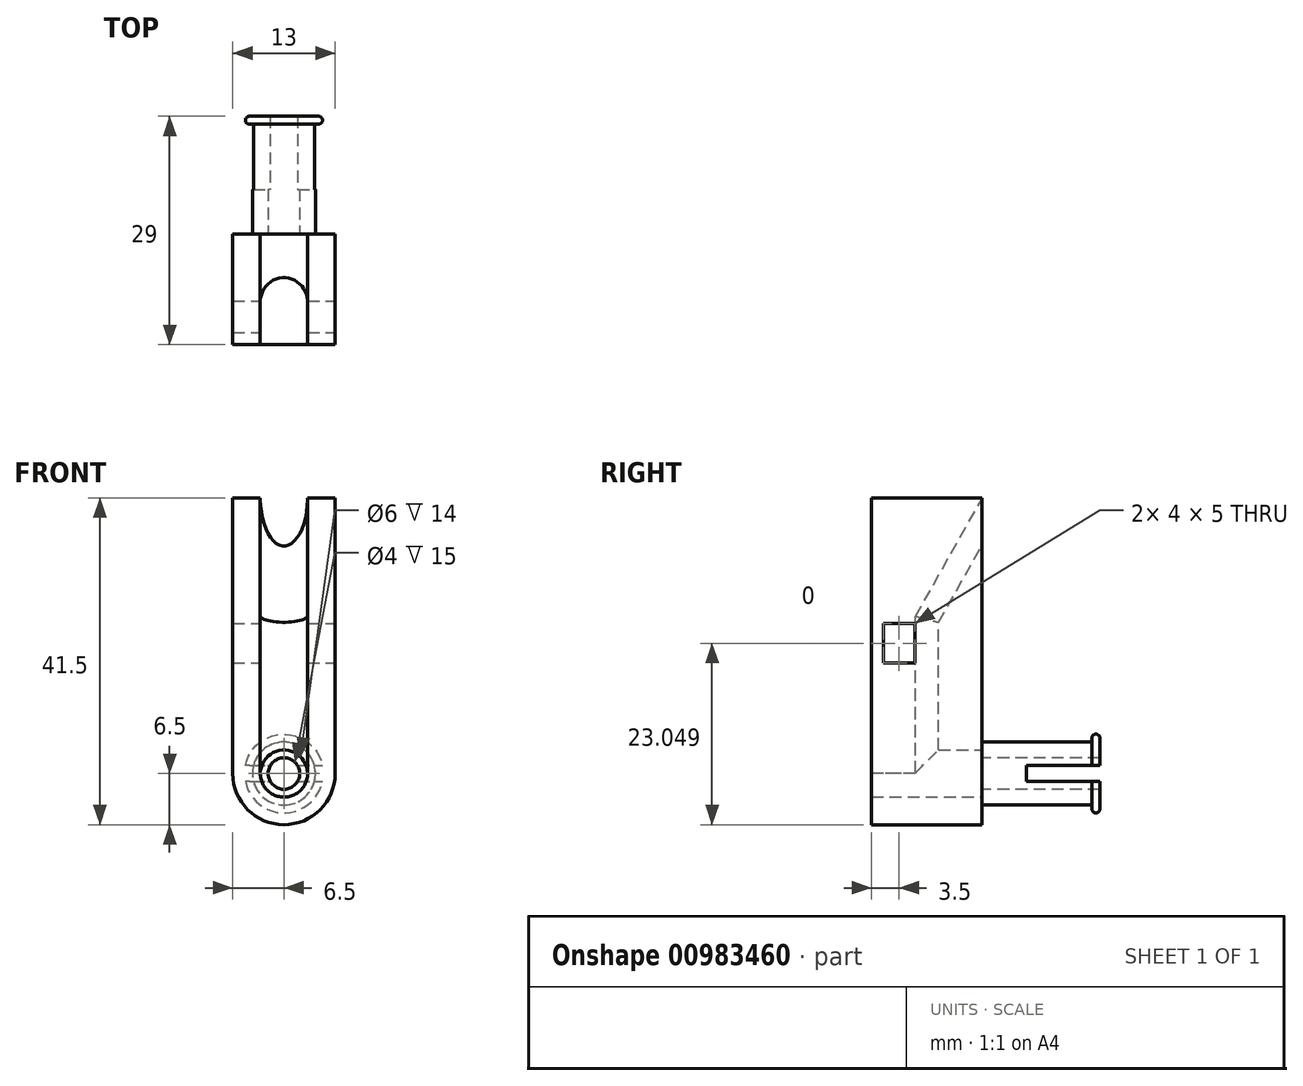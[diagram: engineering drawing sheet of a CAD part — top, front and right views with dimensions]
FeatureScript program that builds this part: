
annotation { "Feature Type Name" : "Feature", "Feature Type Description" : "" }
export const myFeature = defineFeature(function(context is Context, id is Id, definition is map)
    precondition{}
    {
        {
            var Q0;
            Q0=qCreatedBy(makeId("Front.planeOp"),FACE);
            var sketch = newSketch(context, id + "F0", { "sketchPlane" : qUnion([Q0])});
            skCircle(sketch, "E0", {"center": v(0, 0) * mm, "radius": 4 * mm});
            skCircle(sketch, "E1", {"center": v(0, 0) * mm, "radius": 6.5 * mm});
            skPoint(sketch, "E2.middle", {"position": v(0, -6.5) * mm});
            skCircle(sketch, "E3", {"center": v(0, 0) * mm, "radius": 5 * mm});
            skLineSegment(sketch, "E4.bottom", {"start": v(6.5, 0) * mm, "end": v(-6.5, 0) * mm});
            skLineSegment(sketch, "E4.top", {"start": v(6.5, 35) * mm, "end": v(-6.5, 35) * mm});
            skLineSegment(sketch, "E4.left", {"start": v(6.5, 0) * mm, "end": v(6.5, 35) * mm});
            skLineSegment(sketch, "E4.right", {"start": v(-6.5, 0) * mm, "end": v(-6.5, 35) * mm});
            skLineSegment(sketch, "E5.bottom", {"start": v(0, -4) * mm, "end": v(8, -4) * mm});
            skLineSegment(sketch, "E5.top", {"start": v(0, 4) * mm, "end": v(8, 4) * mm});
            skLineSegment(sketch, "E5.left", {"start": v(0, -4) * mm, "end": v(0, 4) * mm});
            skLineSegment(sketch, "E5.right", {"start": v(8, -4) * mm, "end": v(8, 4) * mm});
            skCircle(sketch, "E6", {"center": v(0, 0) * mm, "radius": 3 * mm});
            skCircle(sketch, "E7", {"center": v(4.3, 17.8) * mm, "radius": 1 * mm});
            skCircle(sketch, "E8", {"center": v(3.96, 8.34) * mm, "radius": 1 * mm});
            skCircle(sketch, "E9", {"center": v(0, 0) * mm, "radius": 2 * mm});
            skSolve(sketch);
        }
        {
            var Q0;
            Q0=qCreatedBy(makeId("Right.planeOp"),FACE);
            var sketch = newSketch(context, id + "F1", { "sketchPlane" : qUnion([Q0])});
            skLineSegment(sketch, "E10", {"start": v(0, 40) * mm, "end": v(0, 35) * mm});
            skLineSegment(sketch, "E11", {"start": v(0, 35) * mm, "end": v(-8.5, 20) * mm});
            skLineSegment(sketch, "E12", {"start": v(-8.5, 20) * mm, "end": v(-8.5, 0) * mm});
            skLineSegment(sketch, "E13", {"start": v(-8.5, 0) * mm, "end": v(8.5, 0) * mm});
            skLineSegment(sketch, "E14.left", {"start": v(-6, 2.5) * mm, "end": v(-6, -2.5) * mm});
            skPoint(sketch, "E14.middle", {"position": v(-8.5, 0) * mm});
            skLineSegment(sketch, "E15.bottom", {"start": v(-6, 2.5) * mm, "end": v(-16.53, 2.5) * mm});
            skLineSegment(sketch, "E15.top", {"start": v(-6, -2.5) * mm, "end": v(-16.53, -2.5) * mm});
            skLineSegment(sketch, "E15.right", {"start": v(-16.53, 2.5) * mm, "end": v(-16.53, -2.5) * mm});
            skLineSegment(sketch, "E16.bottom", {"start": v(5.69, 1) * mm, "end": v(25.69, 1) * mm});
            skLineSegment(sketch, "E16.top", {"start": v(5.69, -1) * mm, "end": v(25.69, -1) * mm});
            skLineSegment(sketch, "E16.left", {"start": v(5.69, 1) * mm, "end": v(5.69, -1) * mm});
            skLineSegment(sketch, "E16.right", {"start": v(25.69, 1) * mm, "end": v(25.69, -1) * mm});
            skLineSegment(sketch, "E17.bottom", {"start": v(-8.5, 14.05) * mm, "end": v(-12.5, 14.05) * mm});
            skLineSegment(sketch, "E17.top", {"start": v(-8.5, 19.05) * mm, "end": v(-12.5, 19.05) * mm});
            skLineSegment(sketch, "E17.left", {"start": v(-8.5, 14.05) * mm, "end": v(-8.5, 19.05) * mm});
            skLineSegment(sketch, "E17.right", {"start": v(-12.5, 14.05) * mm, "end": v(-12.5, 19.05) * mm});
            skSolve(sketch);
        }
        {
            var Q0;
            Q0=qCreatedBy(makeId("Top.planeOp"),FACE);
            var sketch = newSketch(context, id + "F2", { "sketchPlane" : qUnion([Q0])});
            skCircle(sketch, "E18", {"center": v(0, -8.5) * mm, "radius": 3 * mm});
            skLineSegment(sketch, "E19.left", {"start": v(0, -5.5) * mm, "end": v(0, -10.5) * mm});
            skLineSegment(sketch, "E20.bottom", {"start": v(-3, -8.42) * mm, "end": v(3, -8.42) * mm});
            skLineSegment(sketch, "E20.top", {"start": v(-3, -23.42) * mm, "end": v(3, -23.42) * mm});
            skLineSegment(sketch, "E20.left", {"start": v(-3, -8.42) * mm, "end": v(-3, -23.42) * mm});
            skLineSegment(sketch, "E20.right", {"start": v(3, -8.42) * mm, "end": v(3, -23.42) * mm});
            skSolve(sketch);
        }
        {
            var Q0;
            Q0=makeQuery(id+"F0.imprint","IMPRINT",FACE,{"disambiguationData":[TD([[makeQuery(id+"F0.imprint","IMPRINT",EDGE,{"derivedFrom":sQuery(id+"F0.wireOp",EDGE,"E0")}),1.0]])]});
            var Q1;
            {var subQ0=sQuery(id+"F0.wireOp",EDGE,"E9");var subQ1=sQuery(id+"F0.wireOp",EDGE,"E4.bottom");var subQ2=makeQuery(id+"F0.imprint","INTERSECT",VERTEX,{"disambiguationData":[OD(1.0)],"derivedFrom":[subQ1,subQ0]});Q1=makeQuery(id+"F0.imprint","IMPRINT",FACE,{"disambiguationData":[TD([[makeQuery(id+"F0.imprint","IMPRINT",EDGE,{"disambiguationData":[TD([[subQ2,-1.0]])],"derivedFrom":subQ1}),-1.0]])]});}
            var Q2;
            {var subQ0=sQuery(id+"F0.wireOp",EDGE,"E9");var subQ1=sQuery(id+"F0.wireOp",EDGE,"E4.bottom");var subQ2=makeQuery(id+"F0.imprint","INTERSECT",VERTEX,{"disambiguationData":[OD(1.0)],"derivedFrom":[subQ1,subQ0]});Q2=makeQuery(id+"F0.imprint","IMPRINT",FACE,{"disambiguationData":[TD([[makeQuery(id+"F0.imprint","IMPRINT",EDGE,{"disambiguationData":[TD([[subQ2,-1.0]])],"derivedFrom":subQ1}),1.0]])]});}
            var Q3;
            {var subQ0=sQuery(id+"F0.wireOp",EDGE,"E6");var subQ1=sQuery(id+"F0.wireOp",EDGE,"E4.bottom");var subQ2=makeQuery(id+"F0.imprint","INTERSECT",VERTEX,{"disambiguationData":[OD(0.0)],"derivedFrom":[subQ1,subQ0]});Q3=makeQuery(id+"F0.imprint","IMPRINT",FACE,{"disambiguationData":[TD([[makeQuery(id+"F0.imprint","IMPRINT",EDGE,{"disambiguationData":[TD([[subQ2,-1.0]])],"derivedFrom":subQ1}),1.0]])]});}
            var Q4;
            {var subQ0=sQuery(id+"F0.wireOp",EDGE,"E6");var subQ1=sQuery(id+"F0.wireOp",EDGE,"E4.bottom");var subQ2=makeQuery(id+"F0.imprint","INTERSECT",VERTEX,{"disambiguationData":[OD(0.0)],"derivedFrom":[subQ1,subQ0]});Q4=makeQuery(id+"F0.imprint","IMPRINT",FACE,{"disambiguationData":[TD([[makeQuery(id+"F0.imprint","IMPRINT",EDGE,{"disambiguationData":[TD([[subQ2,-1.0]])],"derivedFrom":subQ1}),-1.0]])]});}
            extrude(context, id + "F3", {"entities" : qUnion([Q0, Q1, Q2, Q3, Q4]), "oppositeDirection" : true, "depth" : 15 * mm, "offsetDistance" : 25 * mm});
        }
        {
            var Q0;
            Q0=makeQuery(id+"F0.imprint","IMPRINT",FACE,{"disambiguationData":[TD([[makeQuery(id+"F0.imprint","IMPRINT",EDGE,{"derivedFrom":sQuery(id+"F0.wireOp",EDGE,"E1")}),1.0]])]});
            var Q1;
            Q1=makeQuery(id+"F0.imprint","IMPRINT",FACE,{"disambiguationData":[TD([[makeQuery(id+"F0.imprint","IMPRINT",EDGE,{"derivedFrom":sQuery(id+"F0.wireOp",EDGE,"E0")}),-1.0]])]});
            var Q2;
            Q2=makeQuery(id+"F0.imprint","IMPRINT",FACE,{"disambiguationData":[TD([[makeQuery(id+"F0.imprint","IMPRINT",EDGE,{"derivedFrom":sQuery(id+"F0.wireOp",EDGE,"E0")}),1.0]])]});
            var Q3;
            Q3=makeQuery(id+"F0.imprint","IMPRINT",FACE,{"disambiguationData":[TD([[makeQuery(id+"F0.imprint","IMPRINT",EDGE,{"derivedFrom":sQuery(id+"F0.wireOp",EDGE,"E4.top")}),1.0]])]});
            var Q4;
            {var subQ0=sQuery(id+"F0.wireOp",EDGE,"E4.left");var subQ3=sQuery(id+"F0.wireOp",EDGE,"E5.top");var subQ5=makeQuery(id+"F0.imprint","INTERSECT",VERTEX,{"derivedFrom":[subQ0,subQ3]});Q4=makeQuery(id+"F0.imprint","IMPRINT",FACE,{"disambiguationData":[TD([[makeQuery(id+"F0.imprint","IMPRINT",EDGE,{"disambiguationData":[TD([[subQ5,1.0]])],"derivedFrom":subQ3}),-1.0]])]});}
            var Q5;
            Q5=makeQuery(id+"F0.imprint","IMPRINT",FACE,{"disambiguationData":[TD([[makeQuery(id+"F0.imprint","IMPRINT",EDGE,{"derivedFrom":sQuery(id+"F0.wireOp",EDGE,"E7")}),1.0]])]});
            var Q6;
            Q6=makeQuery(id+"F0.imprint","IMPRINT",FACE,{"disambiguationData":[TD([[makeQuery(id+"F0.imprint","IMPRINT",EDGE,{"derivedFrom":sQuery(id+"F0.wireOp",EDGE,"E8")}),1.0]])]});
            extrude(context, id + "F4", {"entities" : qUnion([Q0, Q1, Q2, Q3, Q4, Q5, Q6]), "operationType" : NewBodyOperationType.ADD, "depth" : 14 * mm, "offsetDistance" : 25 * mm});
        }
        {
            var Q0;
            {var subQ1=sQuery(id+"F2.wireOp",EDGE,"E20.top");Q0=makeQuery(id+"F2.imprint","IMPRINT",FACE,{"disambiguationData":[TD([[makeQuery(id+"F2.imprint","IMPRINT",EDGE,{"derivedFrom":subQ1}),1.0]])]});}
            var Q1;
            {var subQ0=sQuery(id+"F2.wireOp",EDGE,"E20.bottom");var subQ1=sQuery(id+"F2.wireOp",EDGE,"E18");var subQ2=makeQuery(id+"F2.imprint","INTERSECT",VERTEX,{"derivedFrom":[subQ1,subQ0]});Q1=makeQuery(id+"F2.imprint","IMPRINT",FACE,{"disambiguationData":[TD([[makeQuery(id+"F2.imprint","IMPRINT",EDGE,{"disambiguationData":[TD([[subQ2,1.0]])],"derivedFrom":subQ1}),1.0]])]});}
            var Q2;
            {var subQ0=sQuery(id+"F2.wireOp",EDGE,"E19.left");var subQ1=sQuery(id+"F2.wireOp",EDGE,"E18");var subQ2=makeQuery(id+"F2.imprint","INTERSECT",VERTEX,{"derivedFrom":[subQ1,subQ0]});Q2=makeQuery(id+"F2.imprint","IMPRINT",FACE,{"disambiguationData":[TD([[makeQuery(id+"F2.imprint","IMPRINT",EDGE,{"disambiguationData":[TD([[subQ2,-1.0]])],"derivedFrom":subQ0}),-1.0]])]});}
            var Q3;
            {var subQ0=sQuery(id+"F2.wireOp",EDGE,"E19.left");var subQ1=sQuery(id+"F2.wireOp",EDGE,"E18");var subQ2=makeQuery(id+"F2.imprint","INTERSECT",VERTEX,{"derivedFrom":[subQ1,subQ0]});Q3=makeQuery(id+"F2.imprint","IMPRINT",FACE,{"disambiguationData":[TD([[makeQuery(id+"F2.imprint","IMPRINT",EDGE,{"disambiguationData":[TD([[subQ2,1.0]])],"derivedFrom":subQ1}),1.0]])]});}
            var Q4;
            Q4=sQuery(id+"F1.wireOp",EDGE,"E12");
            var Q5;
            Q5=sQuery(id+"F1.wireOp",EDGE,"E11");
            var Q6;
            Q6=sQuery(id+"F1.wireOp",EDGE,"E10");
            sweep(context, id + "F5", {"operationType" : NewBodyOperationType.REMOVE, "profiles" : qUnion([Q0, Q1, Q2, Q3]), "path" : qUnion([Q4, Q5, Q6])});
        }
        {
            var Q0;
            {var subQ0=sQuery(id+"F0.wireOp",EDGE,"E5.top");var subQ5=sQuery(id+"F0.wireOp",EDGE,"E3");var subQ6=makeQuery(id+"F0.imprint","INTERSECT",VERTEX,{"derivedFrom":[subQ5,subQ0]});Q0=makeQuery(id+"F0.imprint","IMPRINT",FACE,{"disambiguationData":[TD([[makeQuery(id+"F0.imprint","IMPRINT",EDGE,{"disambiguationData":[TD([[subQ6,1.0]])],"derivedFrom":subQ5}),1.0]])]});}
            var Q1;
            {var subQ0=sQuery(id+"F0.wireOp",EDGE,"E5.top");var subQ5=sQuery(id+"F0.wireOp",EDGE,"E3");var subQ6=makeQuery(id+"F0.imprint","INTERSECT",VERTEX,{"derivedFrom":[subQ5,subQ0]});Q1=makeQuery(id+"F0.imprint","IMPRINT",FACE,{"disambiguationData":[TD([[makeQuery(id+"F0.imprint","IMPRINT",EDGE,{"disambiguationData":[TD([[subQ6,-1.0]])],"derivedFrom":subQ5}),1.0]])]});}
            var Q2;
            {var subQ3=sQuery(id+"F0.wireOp",EDGE,"E4.bottom");var subQ5=sQuery(id+"F0.wireOp",EDGE,"E3");var subQ6=makeQuery(id+"F0.imprint","INTERSECT",VERTEX,{"disambiguationData":[OD(1.0)],"derivedFrom":[subQ5,subQ3]});Q2=makeQuery(id+"F0.imprint","IMPRINT",FACE,{"disambiguationData":[TD([[makeQuery(id+"F0.imprint","IMPRINT",EDGE,{"disambiguationData":[TD([[subQ6,-1.0]])],"derivedFrom":subQ5}),1.0]])]});}
            var Q3;
            {var subQ3=sQuery(id+"F0.wireOp",EDGE,"E4.bottom");var subQ5=sQuery(id+"F0.wireOp",EDGE,"E3");var subQ6=makeQuery(id+"F0.imprint","INTERSECT",VERTEX,{"disambiguationData":[OD(0.0)],"derivedFrom":[subQ5,subQ3]});Q3=makeQuery(id+"F0.imprint","IMPRINT",FACE,{"disambiguationData":[TD([[makeQuery(id+"F0.imprint","IMPRINT",EDGE,{"disambiguationData":[TD([[subQ6,1.0]])],"derivedFrom":subQ5}),1.0]])]});}
            extrude(context, id + "F6", {"entities" : qUnion([Q0, Q1, Q2, Q3]), "operationType" : NewBodyOperationType.ADD, "oppositeDirection" : true, "depth" : 15 * mm, "offsetDistance" : 25 * mm, "hasSecondDirection" : true, "secondDirectionOppositeDirection" : true, "secondDirectionDepth" : 14 * mm});
        }
        {
            var Q0;
            Q0=makeQuery(id+"F6.opExtrude","CAP_EDGE",EDGE,{"disambiguationData":[OSD([sQuery(id+"F0.wireOp",EDGE,"E3")])],"isStart":false});
            var Q1;
            Q1=makeQuery(id+"F6.opExtrude","SWEPT_FACE",FACE,{"disambiguationData":[OSD([sQuery(id+"F0.wireOp",EDGE,"E3")])]});
            fillet(context, id + "F7", {"entities" : qUnion([Q0, Q1]), "radius" : 0.5 * mm, "tangentPropagation" : true, "allowEdgeOverflow" : false});
        }
        {
            var Q0;
            {var subQ3=sQuery(id+"F1.wireOp",EDGE,"E16.bottom");Q0=makeQuery(id+"F1.imprint","IMPRINT",FACE,{"disambiguationData":[TD([[makeQuery(id+"F1.imprint","IMPRINT",EDGE,{"derivedFrom":subQ3}),-1.0]])]});}
            extrude(context, id + "F8", {"entities" : qUnion([Q0]), "operationType" : NewBodyOperationType.REMOVE, "oppositeDirection" : true, "depth" : 25 * mm, "offsetDistance" : 25 * mm, "hasSecondDirection" : true, "secondDirectionOppositeDirection" : false, "secondDirectionDepth" : 25 * mm});
        }
        {
            var Q0;
            Q0=makeQuery(id+"F1.imprint","IMPRINT",FACE,{"disambiguationData":[TD([[makeQuery(id+"F1.imprint","IMPRINT",EDGE,{"derivedFrom":sQuery(id+"F1.wireOp",EDGE,"E17.bottom")}),-1.0]])]});
            extrude(context, id + "F9", {"entities" : qUnion([Q0]), "operationType" : NewBodyOperationType.REMOVE, "oppositeDirection" : true, "depth" : 25 * mm, "offsetDistance" : 25 * mm, "hasSecondDirection" : true, "secondDirectionOppositeDirection" : false, "secondDirectionDepth" : 25 * mm});
        }
    });
